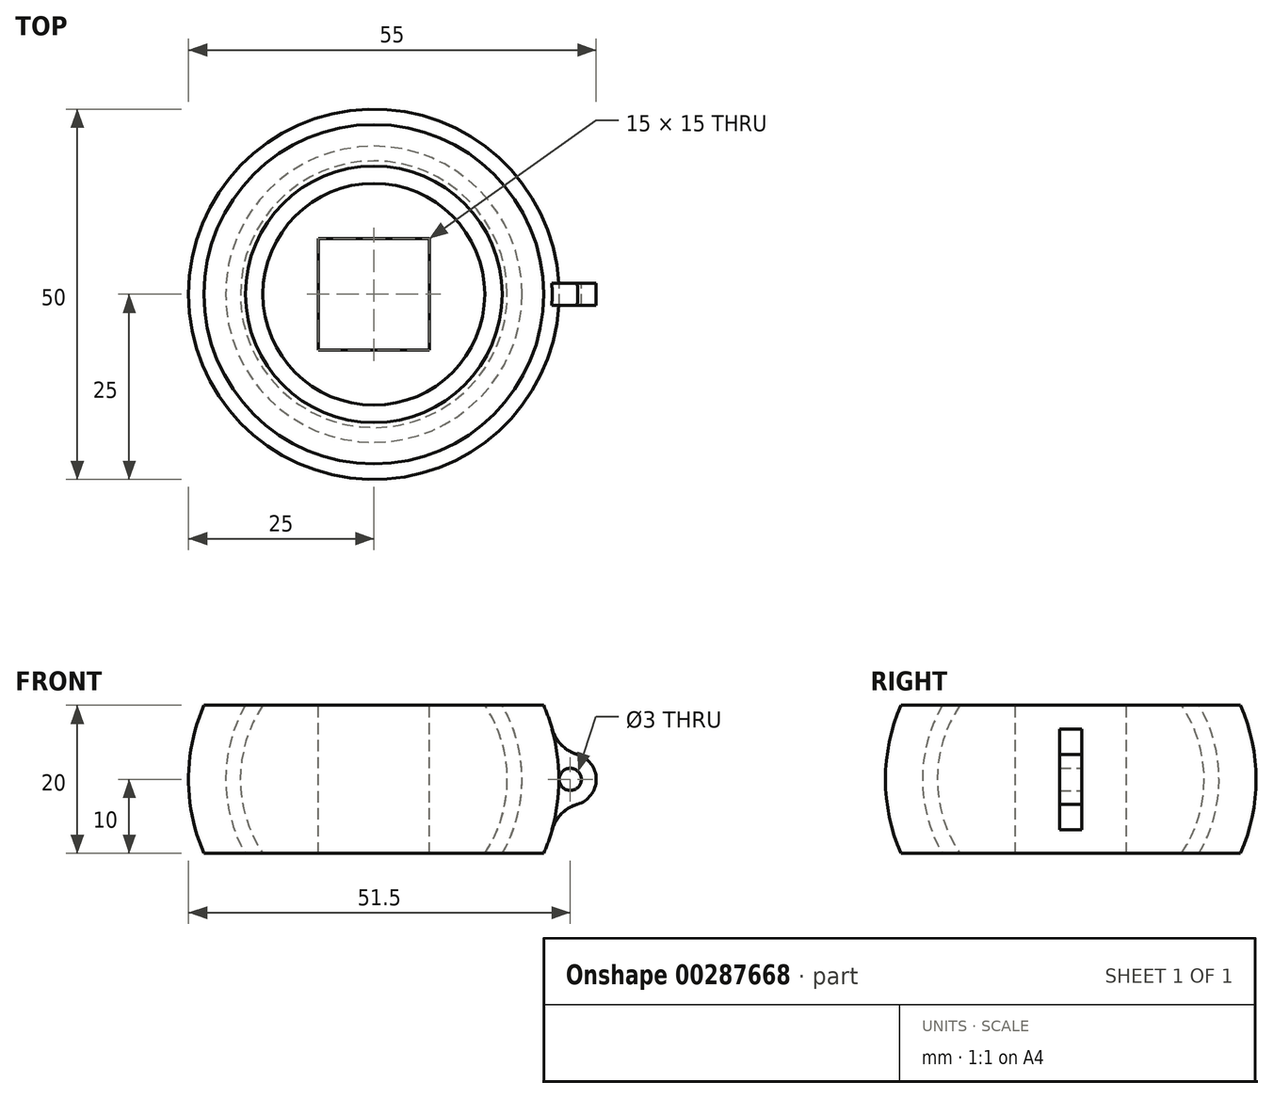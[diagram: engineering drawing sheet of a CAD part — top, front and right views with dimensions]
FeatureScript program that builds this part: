
annotation { "Feature Type Name" : "Feature", "Feature Type Description" : "" }
export const myFeature = defineFeature(function(context is Context, id is Id, definition is map)
    precondition{}
    {
        {
            var Q0;
            Q0=qCreatedBy(makeId("Top.planeOp"),FACE);
            var sketch = newSketch(context, id + "F0", { "sketchPlane" : qUnion([Q0])});
            skCircle(sketch, "E0", {"center": v(0, 0) * mm, "radius": 25 * mm});
            skSolve(sketch);
        }
        {
            var Q0;
            Q0=makeQuery(id+"F0.imprint","IMPRINT",FACE,{"disambiguationData":[TD([[makeQuery(id+"F0.imprint","IMPRINT",EDGE,{"derivedFrom":sQuery(id+"F0.wireOp",EDGE,"E0")}),1.0]])]});
            extrude(context, id + "F1", {"entities" : qUnion([Q0]), "endBound" : BoundingType.SYMMETRIC, "depth" : 20 * mm});
        }
        {
            var Q0;
            Q0=makeQuery(id+"F1.opExtrude","CAP_FACE",FACE,{"disambiguationData":[OSD([sQuery(id+"F0.wireOp",EDGE,"E0")])],"isStart":false});
            var sketch = newSketch(context, id + "F2", { "sketchPlane" : qUnion([Q0])});
            skLineSegment(sketch, "E1.bottom", {"start": v(7.5, 7.5) * mm, "end": v(-7.5, 7.5) * mm});
            skLineSegment(sketch, "E1.top", {"start": v(7.5, -7.5) * mm, "end": v(-7.5, -7.5) * mm});
            skLineSegment(sketch, "E1.left", {"start": v(7.5, 7.5) * mm, "end": v(7.5, -7.5) * mm});
            skLineSegment(sketch, "E1.right", {"start": v(-7.5, 7.5) * mm, "end": v(-7.5, -7.5) * mm});
            skPoint(sketch, "E1.middle", {"position": v(0, 0) * mm});
            skSolve(sketch);
        }
        {
            var Q0;
            Q0=makeQuery(id+"F2.imprint","IMPRINT",FACE,{"disambiguationData":[TD([[makeQuery(id+"F2.imprint","IMPRINT",EDGE,{"derivedFrom":sQuery(id+"F2.wireOp",EDGE,"E1.bottom")}),1.0]])]});
            extrude(context, id + "F3", {"entities" : qUnion([Q0]), "operationType" : NewBodyOperationType.REMOVE, "oppositeDirection" : true, "depth" : 25 * mm});
        }
        {
            var Q0;
            Q0=qCreatedBy(makeId("Front.planeOp"),FACE);
            var sketch = newSketch(context, id + "F4", { "sketchPlane" : qUnion([Q0])});
            skLineSegment(sketch, "E2.0", {"start": v(-25, -10) * mm, "end": v(25, -10) * mm, "construction": true});
            skLineSegment(sketch, "E3.0", {"start": v(-25, 10) * mm, "end": v(25, 10) * mm, "construction": true});
            skArc(sketch, "E4.trimOffspring", {"start": v(-22.91, 10) * mm, "mid": v(-25, 0) * mm, "end": v(-22.91, -10) * mm});
            skLineSegment(sketch, "E5", {"start": v(-22.91, -10) * mm, "end": v(-60, -10) * mm});
            skLineSegment(sketch, "E6", {"start": v(-22.91, 10) * mm, "end": v(-60, 10) * mm});
            skLineSegment(sketch, "E7", {"start": v(-60, -10) * mm, "end": v(-60, 10) * mm});
            skLineSegment(sketch, "E8", {"start": v(0, 0) * mm, "end": v(0, -30.15) * mm, "construction": true});
            skSolve(sketch);
        }
        {
            var Q0;
            Q0=makeQuery(id+"F4.imprint","IMPRINT",FACE,{"disambiguationData":[TD([[makeQuery(id+"F4.imprint","IMPRINT",EDGE,{"derivedFrom":sQuery(id+"F4.wireOp",EDGE,"E4.trimOffspring")}),-1.0]])]});
            var Q1;
            Q1=sQuery(id+"F4.wireOp",EDGE,"E8");
            revolve(context, id + "F5", {"operationType" : NewBodyOperationType.REMOVE, "entities" : qUnion([Q0]), "axis" : qUnion([Q1]), "revolveType" : RevolveType.FULL, "oppositeDirection" : true});
        }
        {
            var Q0;
            Q0=qCreatedBy(makeId("Front.planeOp"),FACE);
            var sketch = newSketch(context, id + "F6", { "sketchPlane" : qUnion([Q0])});
            skArc(sketch, "E9", {"start": v(0, -20) * mm, "mid": v(20, 0) * mm, "end": v(0, 20) * mm});
            skArc(sketch, "E10.0", {"start": v(0, -18) * mm, "mid": v(18, 0) * mm, "end": v(0, 18) * mm});
            skLineSegment(sketch, "E11", {"start": v(0, 0) * mm, "end": v(0, -20) * mm, "construction": true});
            skLineSegment(sketch, "E12", {"start": v(0, 0) * mm, "end": v(0, 23.7) * mm, "construction": true});
            skLineSegment(sketch, "E13", {"start": v(0, -20) * mm, "end": v(0, 20) * mm});
            skSolve(sketch);
        }
        {
            var Q0;
            {var subQ0=sQuery(id+"F6.wireOp",EDGE,"E9");Q0=makeQuery(id+"F6.imprint","IMPRINT",FACE,{"disambiguationData":[TD([[makeQuery(id+"F6.imprint","IMPRINT",EDGE,{"derivedFrom":subQ0}),1.0]])]});}
            var Q1;
            Q1=sQuery(id+"F6.wireOp",EDGE,"E13");
            revolve(context, id + "F7", {"operationType" : NewBodyOperationType.REMOVE, "entities" : qUnion([Q0]), "axis" : qUnion([Q1]), "revolveType" : RevolveType.FULL, "oppositeDirection" : true});
        }
        {
            var Q0;
            Q0=qCreatedBy(makeId("Front.planeOp"),FACE);
            var sketch = newSketch(context, id + "F8", { "sketchPlane" : qUnion([Q0])});
            skCircle(sketch, "E14", {"center": v(26.5, 0) * mm, "radius": 1.5 * mm});
            skCircle(sketch, "E15.0", {"center": v(26.5, 0) * mm, "radius": 3.5 * mm});
            skArc(sketch, "E16", {"start": v(-22.91, 10) * mm, "mid": v(0, -25) * mm, "end": v(22.91, 10) * mm, "construction": true});
            skSolve(sketch);
        }
        {
            var Q0;
            Q0=makeQuery(id+"F8.imprint","IMPRINT",FACE,{"disambiguationData":[TD([[makeQuery(id+"F8.imprint","IMPRINT",EDGE,{"derivedFrom":sQuery(id+"F8.wireOp",EDGE,"E14")}),-1.0]])]});
            extrude(context, id + "F9", {"entities" : qUnion([Q0]), "operationType" : NewBodyOperationType.ADD, "endBound" : BoundingType.SYMMETRIC, "depth" : 3 * mm});
        }
        {
            var Q0;
            Q0=makeQuery(id+"F9.boolean.opBoolean","INTERSECT",EDGE,{"disambiguationData":[OD(0.0)],"derivedFrom":[makeQuery(id+"F5.boolean.opBoolean","COPY",FACE,{"derivedFrom":makeQuery(id+"F5.opRevolve","SWEPT_FACE",FACE,{"disambiguationData":[OSD([sQuery(id+"F4.wireOp",EDGE,"E4.trimOffspring")])]})}),makeQuery(id+"F9.opExtrude","SWEPT_FACE",FACE,{"disambiguationData":[OSD([sQuery(id+"F8.wireOp",EDGE,"E15.0")])]})]});
            var Q1;
            Q1=makeQuery(id+"F9.boolean.opBoolean","INTERSECT",EDGE,{"disambiguationData":[OD(1.0)],"derivedFrom":[makeQuery(id+"F5.boolean.opBoolean","COPY",FACE,{"derivedFrom":makeQuery(id+"F5.opRevolve","SWEPT_FACE",FACE,{"disambiguationData":[OSD([sQuery(id+"F4.wireOp",EDGE,"E4.trimOffspring")])]})}),makeQuery(id+"F9.opExtrude","SWEPT_FACE",FACE,{"disambiguationData":[OSD([sQuery(id+"F8.wireOp",EDGE,"E15.0")])]})]});
            fillet(context, id + "F10", {"entities" : qUnion([Q0, Q1]), "radius" : 5 * mm, "tangentPropagation" : true, "allowEdgeOverflow" : false});
        }
    });
